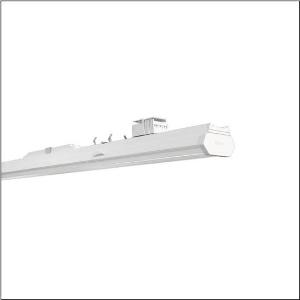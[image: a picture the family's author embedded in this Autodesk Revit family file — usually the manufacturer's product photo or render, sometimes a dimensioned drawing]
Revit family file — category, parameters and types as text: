
# Revit family: licross_r__11_protected_mo_51td12dn495g3s4_8e8e
name_source: partatom
category: Lighting Fixtures
units: mm (PartAtom-declared; Revit-internal decimal feet)

## family parameters
Cut with Voids When Loaded = No
Host = Face
Light Source = No
Part Type = Normal
Room Calculation Point = No
Round Connector Dimension = Use Diameter
Shared = No

## types (1)
- --- (1 x LED, 980 lm, 6.8 W, 4000K)
    Apparent Load = 7 VA
    CIE Flux Codes = 73 92 98 99 100
    Color Rendering = 80
    Color Temperature = 4000K
    Default Elevation = 1800 mm
    Description = Licross® 11 Protected MO, luminaire insert, of sheet steel, galvanised, coil coated, white, length: 1.500mm, width: 90mm, height: 101mm, LED rated luminous flux: 9.980lm, light colour: 840, control gear: DALI 2, with plug, 6-pole, with phase selection, for trunking rail, 9 or 11-core, mains connection: 220..240V, AC, 50/60Hz, rated input power: 61W, for trunking rail, 9-/11-core, halogen-free wiring, for emergency light function, converter,control gear: single battery element, battery: LiFeP04, 9Ah, primary light control with lens, of plastic, primary optical cover: cover, of PMMA, light emission: direct distribution, primary light characteristic: symmetric, protection rating (complete): IP54, insulation class (complete): insulation class I (protective earthing), certification: CE, UKCA, protection symbol: D if used in an environment with non-conductive dust loads with corresponding accessories, impact resistance: IK06, permissible ambient temperature for indoor applications: +5..+35°C, standard: EN 60598-2-22, LABS conformity tested according to VDMA 24364:2018-05, reducing of maximum allowable ambient temperature of 5°C with ceiling mounting, corresponds to IFS (International Featured Standards) requirements for safety and quality in the food industry, packaging unit: 1 piece
    Height = 92 mm
    Lamp = 1 x LED
    Lamp Light Flux = 980 lm
    Lamp Power = 6.8 W
    Lamp count = 1
    Length = 1500 mm
    Luminous efficacy = 144 lm/W
    Manufacturer = Siteco
    ModVariant = No
    Model = 51TD12DN495G3S4
    Mounting Place = Ceiling
    Mounting Type = Pendant
    Number of Poles = 1
    OnlyDefault = Yes
    Power Factor = 1
    Product Name = Licross® 11 Protected MO
    Product group = luminaire insert
    ProductGroupID = 901
    Protection Class = Protection class I
    Protection Degree = IP 54
    RLX_Detail_Level = 1
    RLX_Emergency_Light_Flux = 0 lm
    RLX_Emergency_Type = 0
    RLX_Emergency_Type_DB = No
    RlxData = <blob elided: 24737 chars, md5=c4ecce72>
    Socket = socket
    Standby Power = 0 W
    System Light Flux = 980 lm
    System Power = 7 W
    Type Comments = : emergency light operation: 3 h
    Type Image = l_1256145.jpg
    URL = http://relux.com
    VarID = @adj_041129
    Voltage = 0 V
    Weight = 0.00 kg
    Width = 88 mm

## geometry (parser evidence)
native form markers: Blend x4, Sweep x9
no freeform markers — native parametric forms only
